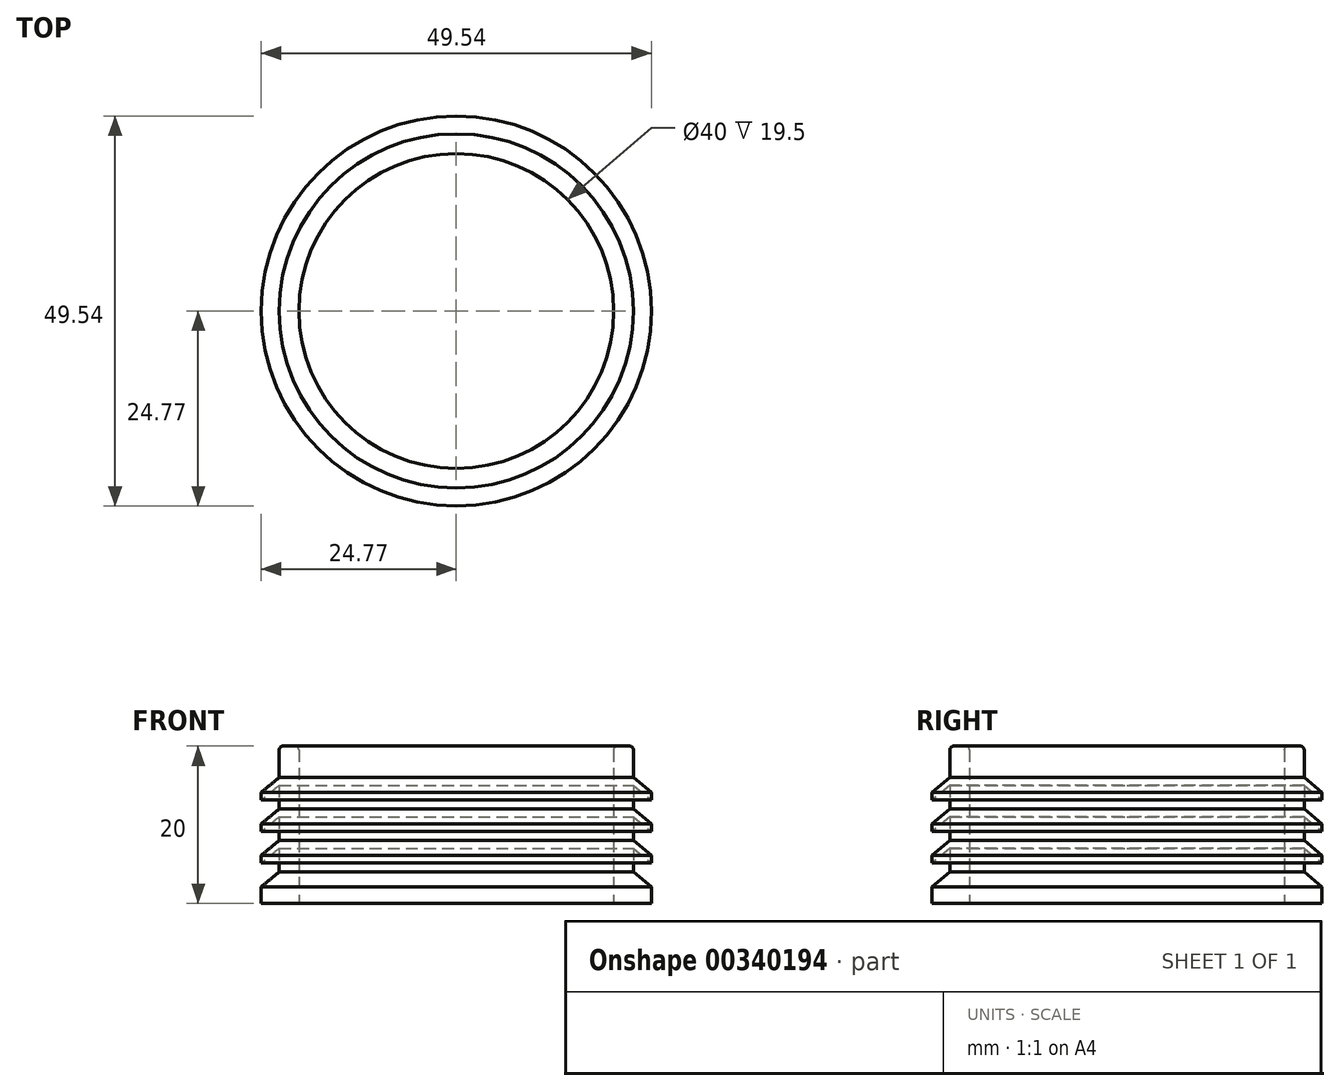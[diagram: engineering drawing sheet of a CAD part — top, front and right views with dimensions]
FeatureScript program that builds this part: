
annotation { "Feature Type Name" : "Feature", "Feature Type Description" : "" }
export const myFeature = defineFeature(function(context is Context, id is Id, definition is map)
    precondition{}
    {
        {
            var Q0;
            Q0=qCreatedBy(makeId("Front.planeOp"),FACE);
            var sketch = newSketch(context, id + "F0", { "sketchPlane" : qUnion([Q0])});
            skLineSegment(sketch, "E0", {"start": v(0, 0) * mm, "end": v(24.77, 0) * mm});
            skLineSegment(sketch, "E1", {"start": v(0, 0) * mm, "end": v(0, 19.11) * mm, "construction": true});
            skLineSegment(sketch, "E2", {"start": v(24.77, 0) * mm, "end": v(24.77, 2.13) * mm});
            skLineSegment(sketch, "E3", {"start": v(24.77, 2.13) * mm, "end": v(22.5, 4) * mm});
            skLineSegment(sketch, "E4", {"start": v(22.5, 4) * mm, "end": v(22.5, 7) * mm});
            skLineSegment(sketch, "E5", {"start": v(22.5, 7) * mm, "end": v(24.77, 5.13) * mm});
            skLineSegment(sketch, "E6", {"start": v(22.5, 7) * mm, "end": v(22.5, 11) * mm});
            skPoint(sketch, "E6.endSnap0", {"position": v(22.5, 5.5) * mm});
            skLineSegment(sketch, "E7", {"start": v(22.5, 11) * mm, "end": v(24.77, 9.13) * mm});
            skLineSegment(sketch, "E8", {"start": v(22.5, 11) * mm, "end": v(22.5, 16) * mm});
            skLineSegment(sketch, "E9", {"start": v(22.5, 16) * mm, "end": v(24.77, 14.13) * mm});
            skLineSegment(sketch, "E10", {"start": v(24.77, 5.13) * mm, "end": v(24.77, 6.13) * mm});
            skLineSegment(sketch, "E11", {"start": v(24.77, 6.13) * mm, "end": v(22.5, 8) * mm});
            skLineSegment(sketch, "E12", {"start": v(24.77, 9.13) * mm, "end": v(24.77, 10.13) * mm});
            skLineSegment(sketch, "E13", {"start": v(24.77, 10.13) * mm, "end": v(22.5, 12) * mm});
            skLineSegment(sketch, "E14", {"start": v(24.77, 13.13) * mm, "end": v(24.77, 14.13) * mm});
            skLineSegment(sketch, "E15", {"start": v(24.77, 13.13) * mm, "end": v(22.5, 15) * mm});
            skLineSegment(sketch, "E16", {"start": v(22.5, 16) * mm, "end": v(22.5, 15) * mm});
            skLineSegment(sketch, "E17", {"start": v(22.5, 16) * mm, "end": v(22.5, 19.5) * mm});
            skLineSegment(sketch, "E18", {"start": v(22, 20) * mm, "end": v(20.5, 20) * mm});
            skLineSegment(sketch, "E19", {"start": v(20, 19.5) * mm, "end": v(20, 0) * mm});
            skPoint(sketch, "E20.visualSharp", {"position": v(20, 20) * mm});
            skArc(sketch, "E20.filletArc", {"start": v(20.5, 20) * mm, "mid": v(20.15, 19.85) * mm, "end": v(20, 19.5) * mm});
            skPoint(sketch, "E21.visualSharp", {"position": v(22.5, 20) * mm});
            skArc(sketch, "E21.filletArc", {"start": v(22.5, 19.5) * mm, "mid": v(22.35, 19.85) * mm, "end": v(22, 20) * mm});
            skSolve(sketch);
        }
        {
            var Q0;
            {var subQ7=sQuery(id+"F0.wireOp",EDGE,"E2");Q0=makeQuery(id+"F0.imprint","IMPRINT",FACE,{"disambiguationData":[TD([[makeQuery(id+"F0.imprint","IMPRINT",EDGE,{"derivedFrom":subQ7}),1.0]])]});}
            var Q1;
            {var subQ0=sQuery(id+"F0.wireOp",EDGE,"E5");Q1=makeQuery(id+"F0.imprint","IMPRINT",FACE,{"disambiguationData":[TD([[makeQuery(id+"F0.imprint","IMPRINT",EDGE,{"derivedFrom":subQ0}),1.0]])]});}
            var Q2;
            {var subQ0=sQuery(id+"F0.wireOp",EDGE,"E7");Q2=makeQuery(id+"F0.imprint","IMPRINT",FACE,{"disambiguationData":[TD([[makeQuery(id+"F0.imprint","IMPRINT",EDGE,{"derivedFrom":subQ0}),1.0]])]});}
            var Q3;
            Q3=makeQuery(id+"F0.imprint","IMPRINT",FACE,{"disambiguationData":[TD([[makeQuery(id+"F0.imprint","IMPRINT",EDGE,{"derivedFrom":sQuery(id+"F0.wireOp",EDGE,"E9")}),-1.0]])]});
            var Q4;
            Q4=sQuery(id+"F0.wireOp",EDGE,"E1");
            revolve(context, id + "F1", {"entities" : qUnion([Q0, Q1, Q2, Q3]), "axis" : qUnion([Q4]), "revolveType" : RevolveType.FULL});
        }
    });
